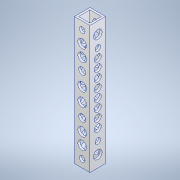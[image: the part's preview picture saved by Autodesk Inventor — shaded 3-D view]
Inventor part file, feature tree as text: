
AUTODESK INVENTOR PART (.ipt)
format: ipt  version: 2020.3 (Build 243373000, 373)  size: 251,392 bytes
history: native  units: mm
features: sketch x7, hole x6, other x1, extrude x1
ambient origin geometry x8: Origin, YZ Plane, XZ Plane, XY Plane, X Axis, Y Axis, Z Axis, Center Point
bodies: Body1 (feature_tree)
feature tree (15):
  other  "ソリッド1"
  extrude  "押し出し1"  Depth=9.0mm
  hole  "穴1"  [1 undecoded]
  hole  "穴2"  [1 undecoded]
  hole  "穴3"  [1 undecoded]
  hole  "穴4"  [1 undecoded]
  hole  "穴5"  [1 undecoded]
  hole  "穴6"  [1 undecoded]
  sketch  "スケッチ1"
  sketch  "スケッチ2"
  sketch  "スケッチ3"
  sketch  "スケッチ4"
  sketch  "スケッチ5"
  sketch  "スケッチ6"
  sketch  "スケッチ7"
note: 6 required parameter values undecoded (feature->parameter linkage not recoverable at this tier; creation-order binding heuristic only, values carry confidence <= 0.55)
